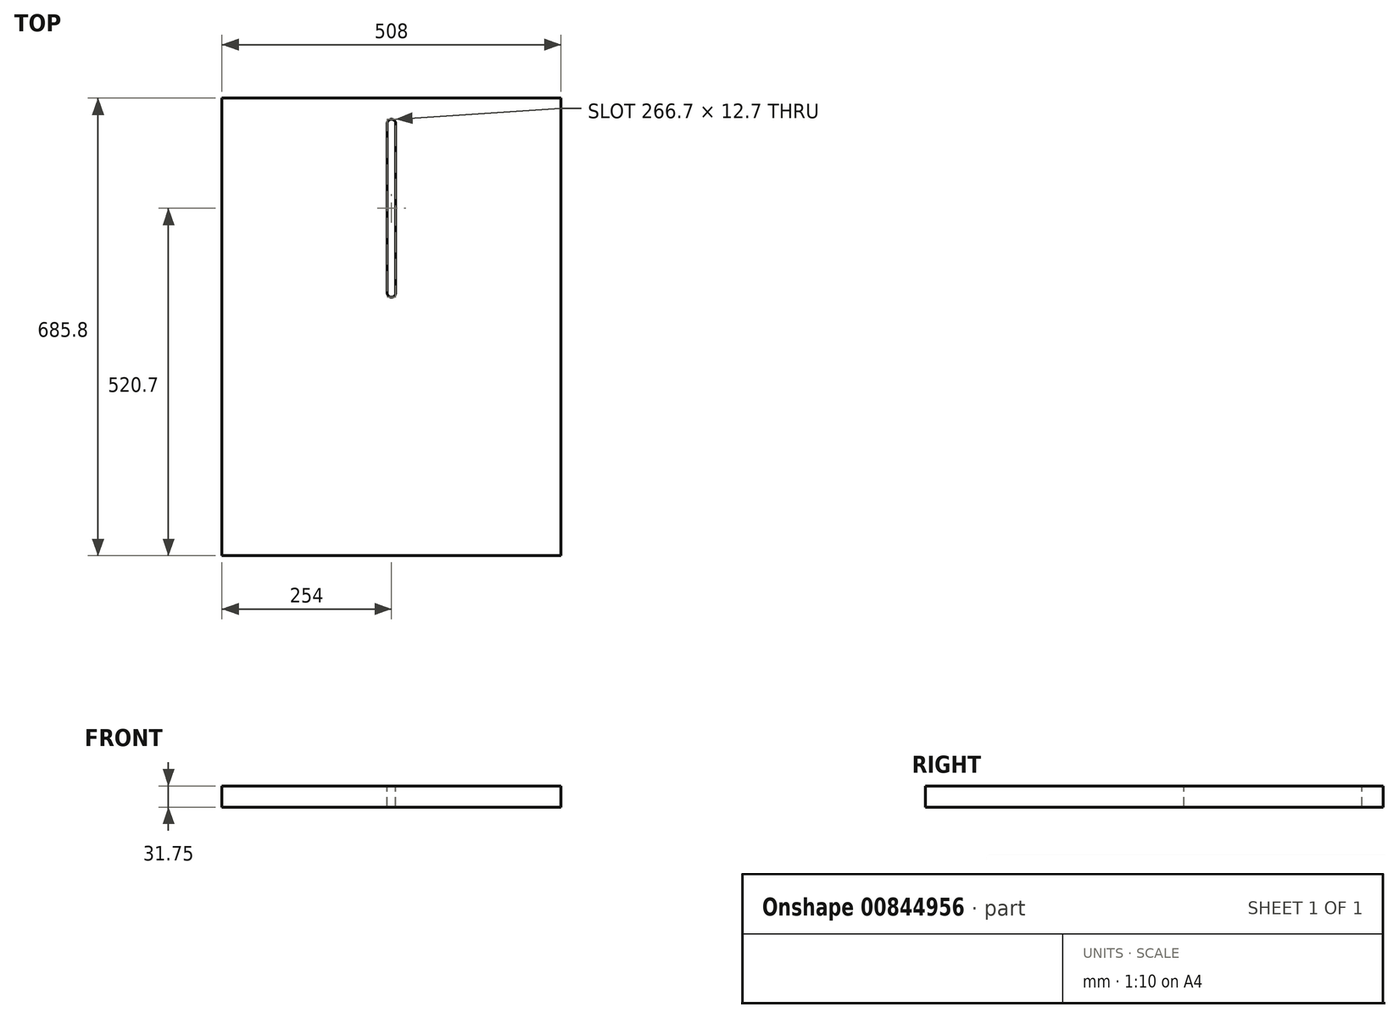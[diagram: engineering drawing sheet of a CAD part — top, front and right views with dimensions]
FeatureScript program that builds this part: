
annotation { "Feature Type Name" : "Feature", "Feature Type Description" : "" }
export const myFeature = defineFeature(function(context is Context, id is Id, definition is map)
    precondition{}
    {
        {
            var Q0;
            Q0=qCreatedBy(makeId("Top.planeOp"),FACE);
            var sketch = newSketch(context, id + "F0", { "sketchPlane" : qUnion([Q0])});
            skLineSegment(sketch, "E0.bottom", {"start": v(254, 342.9) * mm, "end": v(-254, 342.9) * mm});
            skLineSegment(sketch, "E0.top", {"start": v(254, -342.9) * mm, "end": v(-254, -342.9) * mm});
            skLineSegment(sketch, "E0.left", {"start": v(254, 342.9) * mm, "end": v(254, -342.9) * mm});
            skLineSegment(sketch, "E0.right", {"start": v(-254, 342.9) * mm, "end": v(-254, -342.9) * mm});
            skPoint(sketch, "E0.middle", {"position": v(0, 0) * mm});
            skSolve(sketch);
        }
        {
            var Q0;
            Q0=makeQuery(id+"F0.imprint","IMPRINT",FACE,{"disambiguationData":[TD([[makeQuery(id+"F0.imprint","IMPRINT",EDGE,{"derivedFrom":sQuery(id+"F0.wireOp",EDGE,"E0.bottom")}),1.0]])]});
            extrude(context, id + "F1", {"entities" : qUnion([Q0]), "depth" : 31.75 * mm, "offsetDistance" : 25.4 * mm});
        }
        {
            var Q0;
            Q0=makeQuery(id+"F1.opExtrude","CAP_FACE",FACE,{"disambiguationData":[OSD([sQuery(id+"F0.wireOp",EDGE,"E0.bottom"),sQuery(id+"F0.wireOp",EDGE,"E0.top"),sQuery(id+"F0.wireOp",EDGE,"E0.left"),sQuery(id+"F0.wireOp",EDGE,"E0.right")])],"isStart":false});
            var sketch = newSketch(context, id + "F2", { "sketchPlane" : qUnion([Q0])});
            skPoint(sketch, "E1", {"position": v(0, 304.8) * mm});
            skCircle(sketch, "E2", {"center": v(0, 304.8) * mm, "radius": 6.35 * mm});
            skPoint(sketch, "E3", {"position": v(0, 50.8) * mm});
            skCircle(sketch, "E4", {"center": v(0, 50.8) * mm, "radius": 6.35 * mm});
            skLineSegment(sketch, "E5", {"start": v(-6.35, 304.8) * mm, "end": v(-6.35, 50.8) * mm});
            skLineSegment(sketch, "E6", {"start": v(6.35, 304.8) * mm, "end": v(6.35, 50.8) * mm});
            skSolve(sketch);
        }
        {
            var Q0;
            {var subQ0=sQuery(id+"F2.wireOp",EDGE,"E2");var subQ1=makeQuery(id+"F2.imprint","INTERSECT",VERTEX,{"derivedFrom":[subQ0,sQuery(id+"F2.wireOp",EDGE,"E5")]});Q0=makeQuery(id+"F2.imprint","IMPRINT",FACE,{"disambiguationData":[TD([[makeQuery(id+"F2.imprint","IMPRINT",EDGE,{"disambiguationData":[TD([[subQ1,1.0]])],"derivedFrom":subQ0}),1.0]])]});}
            var Q1;
            {var subQ0=sQuery(id+"F2.wireOp",EDGE,"E4");var subQ1=makeQuery(id+"F2.imprint","INTERSECT",VERTEX,{"derivedFrom":[subQ0,sQuery(id+"F2.wireOp",EDGE,"E5")]});Q1=makeQuery(id+"F2.imprint","IMPRINT",FACE,{"disambiguationData":[TD([[makeQuery(id+"F2.imprint","IMPRINT",EDGE,{"disambiguationData":[TD([[subQ1,1.0]])],"derivedFrom":subQ0}),1.0]])]});}
            var Q2;
            {var subQ0=sQuery(id+"F2.wireOp",EDGE,"E5");Q2=makeQuery(id+"F2.imprint","IMPRINT",FACE,{"disambiguationData":[TD([[makeQuery(id+"F2.imprint","IMPRINT",EDGE,{"derivedFrom":subQ0}),1.0]])]});}
            extrude(context, id + "F3", {"entities" : qUnion([Q0, Q1, Q2]), "operationType" : NewBodyOperationType.REMOVE, "oppositeDirection" : true, "depth" : 31.75 * mm, "offsetDistance" : 25.4 * mm});
        }
    });
